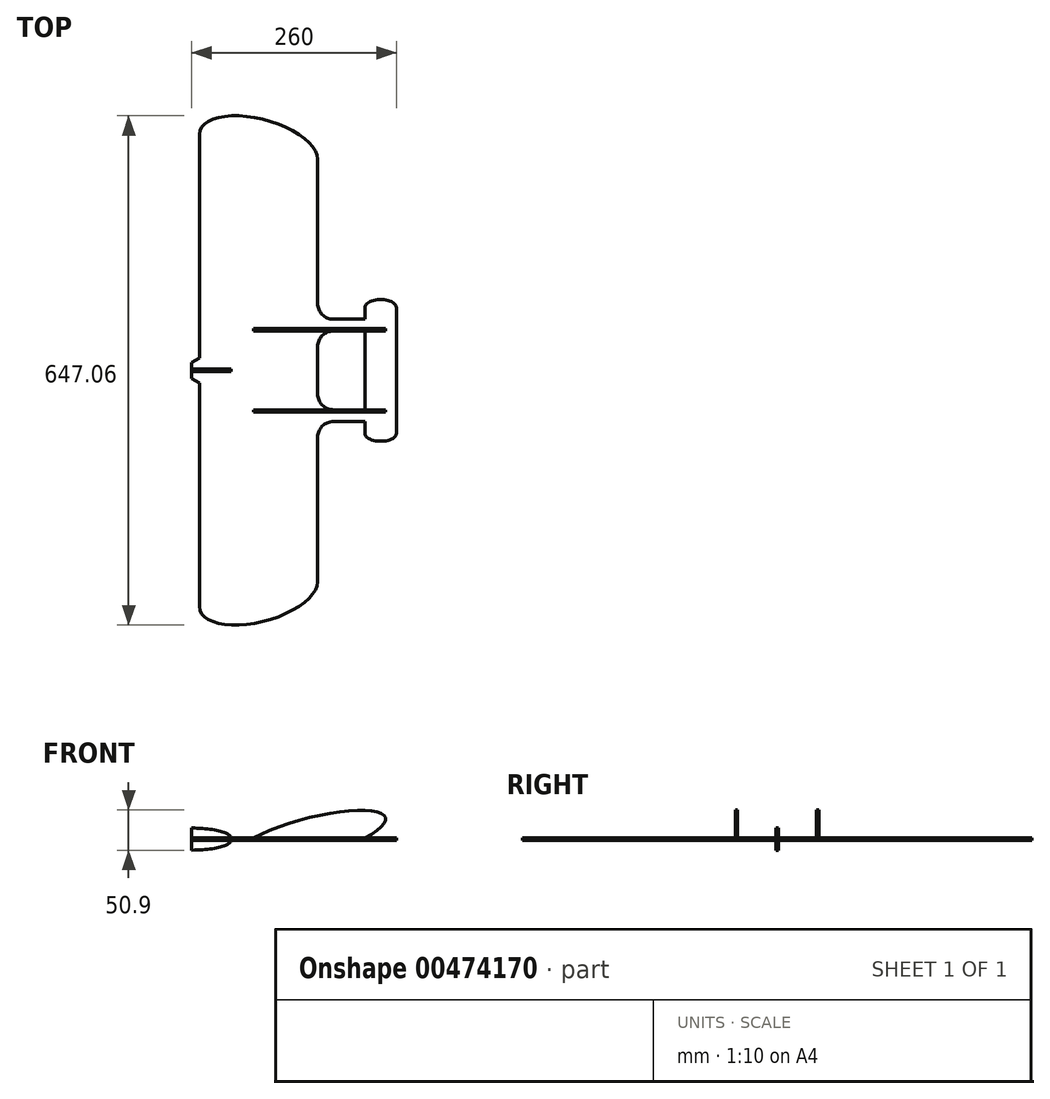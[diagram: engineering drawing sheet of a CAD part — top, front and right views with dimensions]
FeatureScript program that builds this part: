
annotation { "Feature Type Name" : "Feature", "Feature Type Description" : "" }
export const myFeature = defineFeature(function(context is Context, id is Id, definition is map)
    precondition{}
    {
        {
            var Q0;
            Q0=qCreatedBy(makeId("Top.planeOp"),FACE);
            var sketch = newSketch(context, id + "F0", { "sketchPlane" : qUnion([Q0])});
            skLineSegment(sketch, "E0", {"start": v(0, 0) * mm, "end": v(0, 10) * mm});
            skLineSegment(sketch, "E1", {"start": v(0, 10) * mm, "end": v(10, 15.77) * mm});
            skLineSegment(sketch, "E2", {"start": v(10, 15.77) * mm, "end": v(10, 300) * mm});
            skLineSegment(sketch, "E3", {"start": v(10, 300) * mm, "end": v(135.95, 300) * mm});
            skLineSegment(sketch, "E4", {"start": v(160, 268.56) * mm, "end": v(160, 65) * mm});
            skLineSegment(sketch, "E5", {"start": v(160, 65) * mm, "end": v(220, 65) * mm});
            skLineSegment(sketch, "E6", {"start": v(220, 65) * mm, "end": v(220, 50) * mm});
            skLineSegment(sketch, "E7", {"start": v(220, 50) * mm, "end": v(160, 50) * mm});
            skLineSegment(sketch, "E8", {"start": v(160, 50) * mm, "end": v(160, 0) * mm});
            skLineSegment(sketch, "E9", {"start": v(160, 0) * mm, "end": v(0, 0) * mm});
            skEllipse(sketch, "E10", {"center": v(85, 284.28) * mm, "majorRadius": 77.08 * mm, "minorRadius": 35 * mm, "majorAxis": v(0.97, -0.26)});
            skLineSegment(sketch, "E11", {"start": v(85, 284.28) * mm, "end": v(159.45, 264.33) * mm, "construction": true});
            skLineSegment(sketch, "E12", {"start": v(85, 284.28) * mm, "end": v(94.06, 318.09) * mm, "construction": true});
            skPoint(sketch, "E13.orphan", {"position": v(160, 300) * mm});
            skSolve(sketch);
        }
        {
            var Q0;
            {var subQ0=sQuery(id+"F0.wireOp",EDGE,"E3");Q0=makeQuery(id+"F0.imprint","IMPRINT",FACE,{"disambiguationData":[TD([[makeQuery(id+"F0.imprint","IMPRINT",EDGE,{"derivedFrom":subQ0}),1.0]])]});}
            var Q1;
            {var subQ0=sQuery(id+"F0.wireOp",EDGE,"E3");Q1=makeQuery(id+"F0.imprint","IMPRINT",FACE,{"disambiguationData":[TD([[makeQuery(id+"F0.imprint","IMPRINT",EDGE,{"derivedFrom":subQ0}),-1.0]])]});}
            var Q2;
            Q2=makeQuery(id+"F0.imprint","IMPRINT",FACE,{"disambiguationData":[TD([[makeQuery(id+"F0.imprint","IMPRINT",EDGE,{"derivedFrom":sQuery(id+"F0.wireOp",EDGE,"E0")}),-1.0]])]});
            extrude(context, id + "F1", {"entities" : qUnion([Q0, Q1, Q2]), "depth" : 3 * mm, "symmetric" : true});
        }
        {
            var Q0;
            Q0=makeQuery(id+"F1.opExtrude","SWEPT_BODY",BODY,{"disambiguationData":[OSD([sQuery(id+"F0.wireOp",EDGE,"E0"),sQuery(id+"F0.wireOp",EDGE,"E1"),sQuery(id+"F0.wireOp",EDGE,"E2"),sQuery(id+"F0.wireOp",EDGE,"E4"),sQuery(id+"F0.wireOp",EDGE,"E5"),sQuery(id+"F0.wireOp",EDGE,"E6"),sQuery(id+"F0.wireOp",EDGE,"E7"),sQuery(id+"F0.wireOp",EDGE,"E8"),sQuery(id+"F0.wireOp",EDGE,"E9"),sQuery(id+"F0.wireOp",EDGE,"E10")])]});
            var Q1;
            Q1=qCreatedBy(makeId("Front.planeOp"),FACE);
            mirror(context, id + "F2", {"operationType" : NewBodyOperationType.ADD, "entities" : qUnion([Q0]), "mirrorPlane" : qUnion([Q1])});
        }
        {
            var Q0;
            Q0=qCreatedBy(makeId("Front.planeOp"),FACE);
            var sketch = newSketch(context, id + "F3", { "sketchPlane" : qUnion([Q0])});
            skLineSegment(sketch, "E14", {"start": v(160, 1.5) * mm, "end": v(0, 1.5) * mm});
            skLineSegment(sketch, "E15", {"start": v(0, 1.5) * mm, "end": v(0, 14) * mm});
            skEllipse(sketch, "E16", {"center": v(0, 1.5) * mm, "majorRadius": 12.5 * mm, "minorRadius": 50 * mm, "majorAxis": v(0, 1)});
            skLineSegment(sketch, "E17", {"start": v(0, 1.5) * mm, "end": v(50, 1.5) * mm});
            skSolve(sketch);
        }
        {
            var Q0;
            {var subQ0=sQuery(id+"F3.wireOp",EDGE,"E15");Q0=makeQuery(id+"F3.imprint","IMPRINT",FACE,{"disambiguationData":[TD([[makeQuery(id+"F3.imprint","IMPRINT",EDGE,{"derivedFrom":subQ0}),-1.0]])]});}
            extrude(context, id + "F4", {"entities" : qUnion([Q0]), "depth" : 3 * mm, "symmetric" : true});
        }
        {
            var Q0;
            Q0=makeQuery(id+"F4.opExtrude","SWEPT_BODY",BODY,{"disambiguationData":[OSD([sQuery(id+"F3.wireOp",EDGE,"E15"),sQuery(id+"F3.wireOp",EDGE,"E16"),sQuery(id+"F3.wireOp",EDGE,"E17")])]});
            var Q1;
            Q1=qCreatedBy(makeId("Top.planeOp"),FACE);
            mirror(context, id + "F5", {"entities" : qUnion([Q0]), "mirrorPlane" : qUnion([Q1])});
        }
        {
            var Q0;
            Q0=makeQuery(id+"F1.opExtrude","SWEPT_FACE",FACE,{"disambiguationData":[OSD([sQuery(id+"F0.wireOp",EDGE,"E7")])]});
            var sketch = newSketch(context, id + "F6", { "sketchPlane" : qUnion([Q0])});
            skEllipse(sketch, "E18", {"center": v(149.37, 1.5) * mm, "majorRadius": 100 * mm, "minorRadius": 25 * mm, "majorAxis": v(0.97, 0.26)});
            skLineSegment(sketch, "E19", {"start": v(149.37, 1.5) * mm, "end": v(142.9, 25.65) * mm, "construction": true});
            skLineSegment(sketch, "E20", {"start": v(149.37, 1.5) * mm, "end": v(245.97, 27.38) * mm, "construction": true});
            skLineSegment(sketch, "E21", {"start": v(220, 1.5) * mm, "end": v(78.75, 1.5) * mm});
            skSolve(sketch);
        }
        {
            var Q0;
            {var subQ0=sQuery(id+"F6.wireOp",EDGE,"E21");var subQ1=sQuery(id+"F6.wireOp",EDGE,"E18");var subQ4=makeQuery(id+"F6.imprint","INTERSECT",VERTEX,{"derivedFrom":[subQ1,subQ0]});Q0=makeQuery(id+"F6.imprint","IMPRINT",FACE,{"disambiguationData":[TD([[makeQuery(id+"F6.imprint","IMPRINT",EDGE,{"disambiguationData":[TD([[subQ4,1.0]])],"derivedFrom":subQ0}),-1.0]])]});}
            extrude(context, id + "F7", {"entities" : qUnion([Q0]), "oppositeDirection" : true, "depth" : 3 * mm});
        }
        {
            var Q0;
            Q0=makeQuery(id+"F7.opExtrude","SWEPT_BODY",BODY,{"disambiguationData":[OSD([sQuery(id+"F6.wireOp",EDGE,"E18"),sQuery(id+"F6.wireOp",EDGE,"E21")])]});
            var Q1;
            Q1=qCreatedBy(makeId("Front.planeOp"),FACE);
            mirror(context, id + "F8", {"entities" : qUnion([Q0]), "mirrorPlane" : qUnion([Q1])});
        }
        {
            var Q0;
            Q0=makeQuery(id+"F2.opPattern","COPY",EDGE,{"derivedFrom":makeQuery(id+"F1.opExtrude","SWEPT_EDGE",EDGE,{"disambiguationData":[OSD([sQuery(id+"F0.wireOp",EDGE,"E4"),sQuery(id+"F0.wireOp",EDGE,"E5")])]}),"instanceName":"1"});
            var Q1;
            Q1=makeQuery(id+"F1.opExtrude","SWEPT_EDGE",EDGE,{"disambiguationData":[OSD([sQuery(id+"F0.wireOp",EDGE,"E4"),sQuery(id+"F0.wireOp",EDGE,"E5")])]});
            var Q2;
            Q2=makeQuery(id+"F2.opPattern","COPY",EDGE,{"derivedFrom":makeQuery(id+"F1.opExtrude","SWEPT_EDGE",EDGE,{"disambiguationData":[OSD([sQuery(id+"F0.wireOp",EDGE,"E7"),sQuery(id+"F0.wireOp",EDGE,"E8")])]}),"instanceName":"1"});
            var Q3;
            Q3=makeQuery(id+"F1.opExtrude","SWEPT_EDGE",EDGE,{"disambiguationData":[OSD([sQuery(id+"F0.wireOp",EDGE,"E7"),sQuery(id+"F0.wireOp",EDGE,"E8")])]});
            fillet(context, id + "F9", {"entities" : qUnion([Q0, Q1, Q2, Q3]), "radius" : 20 * mm, "tangentPropagation" : true, "allowEdgeOverflow" : false});
        }
        {
            var Q0;
            Q0=qCreatedBy(makeId("Top.planeOp"),FACE);
            var sketch = newSketch(context, id + "F10", { "sketchPlane" : qUnion([Q0])});
            skLineSegment(sketch, "E22.bottom", {"start": v(220, 80) * mm, "end": v(260, 80) * mm});
            skLineSegment(sketch, "E22.top", {"start": v(220, 0) * mm, "end": v(260, 0) * mm});
            skLineSegment(sketch, "E22.left", {"start": v(220, 80) * mm, "end": v(220, 0) * mm});
            skLineSegment(sketch, "E22.right", {"start": v(260, 80) * mm, "end": v(260, 0) * mm});
            skEllipse(sketch, "E23", {"center": v(240, 80) * mm, "majorRadius": 20 * mm, "minorRadius": 10 * mm, "majorAxis": v(-1, 0)});
            skSolve(sketch);
        }
        {
            var Q0;
            Q0 = qSketchRegion(id + "F10", true);
            extrude(context, id + "F11", {"entities" : qUnion([Q0]), "depth" : 3 * mm, "symmetric" : true});
        }
        {
            var Q0;
            Q0=makeQuery(id+"F11.opExtrude","SWEPT_BODY",BODY,{"disambiguationData":[OSD([sQuery(id+"F10.wireOp",EDGE,"E22.top"),sQuery(id+"F10.wireOp",EDGE,"E22.left"),sQuery(id+"F10.wireOp",EDGE,"E22.right"),sQuery(id+"F10.wireOp",EDGE,"E23")])]});
            var Q1;
            Q1=qCreatedBy(makeId("Front.planeOp"),FACE);
            mirror(context, id + "F12", {"operationType" : NewBodyOperationType.ADD, "entities" : qUnion([Q0]), "mirrorPlane" : qUnion([Q1])});
        }
    });
